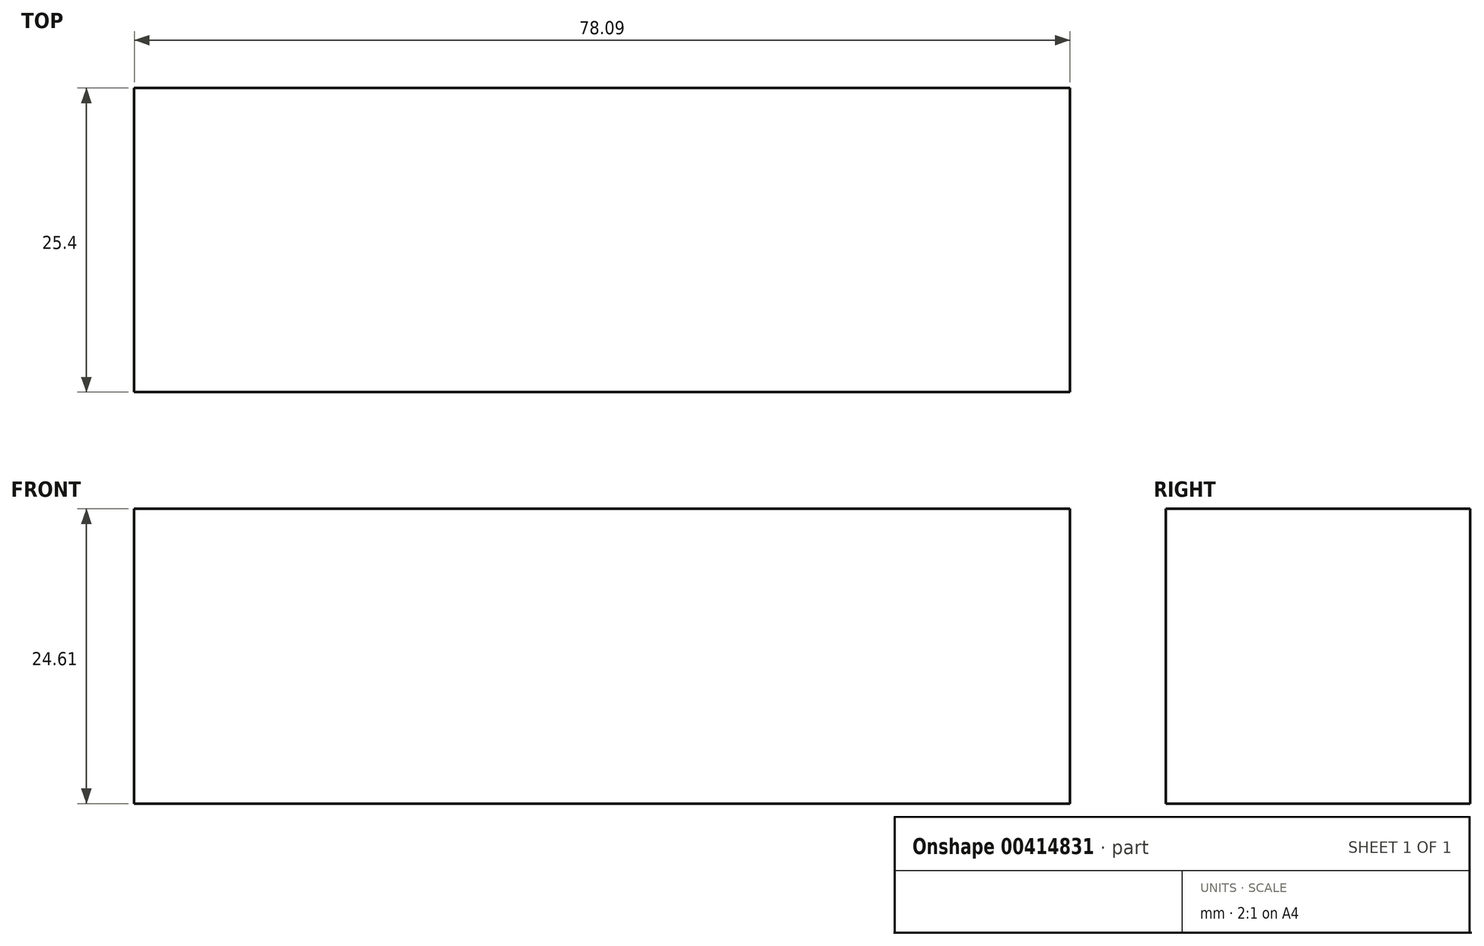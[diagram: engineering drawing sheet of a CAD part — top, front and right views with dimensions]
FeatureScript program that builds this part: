
annotation { "Feature Type Name" : "Feature", "Feature Type Description" : "" }
export const myFeature = defineFeature(function(context is Context, id is Id, definition is map)
    precondition{}
    {
        {
            var Q0;
            Q0=qCreatedBy(makeId("Front.planeOp"),FACE);
            var sketch = newSketch(context, id + "F0", { "sketchPlane" : qUnion([Q0])});
            skLineSegment(sketch, "E0", {"start": v(-37.7, -24.6) * mm, "end": v(-37.7, 0) * mm});
            skLineSegment(sketch, "E1", {"start": v(-37.7, -24.6) * mm, "end": v(0, -24.6) * mm});
            skLineSegment(sketch, "E2", {"start": v(0, -24.6) * mm, "end": v(40.4, -24.6) * mm});
            skLineSegment(sketch, "E3", {"start": v(40.4, 0) * mm, "end": v(40.4, -24.6) * mm});
            skLineSegment(sketch, "E4", {"start": v(40.4, 0) * mm, "end": v(-37.7, 0) * mm});
            skSolve(sketch);
        }
        {
            var Q0;
            Q0=makeQuery(id+"F0.imprint","IMPRINT",FACE,{"disambiguationData":[TD([[makeQuery(id+"F0.imprint","IMPRINT",EDGE,{"derivedFrom":sQuery(id+"F0.wireOp",EDGE,"E0")}),-1.0]])]});
            extrude(context, id + "F1", {"entities" : qUnion([Q0]), "depth" : 25.4 * mm});
        }
    });
